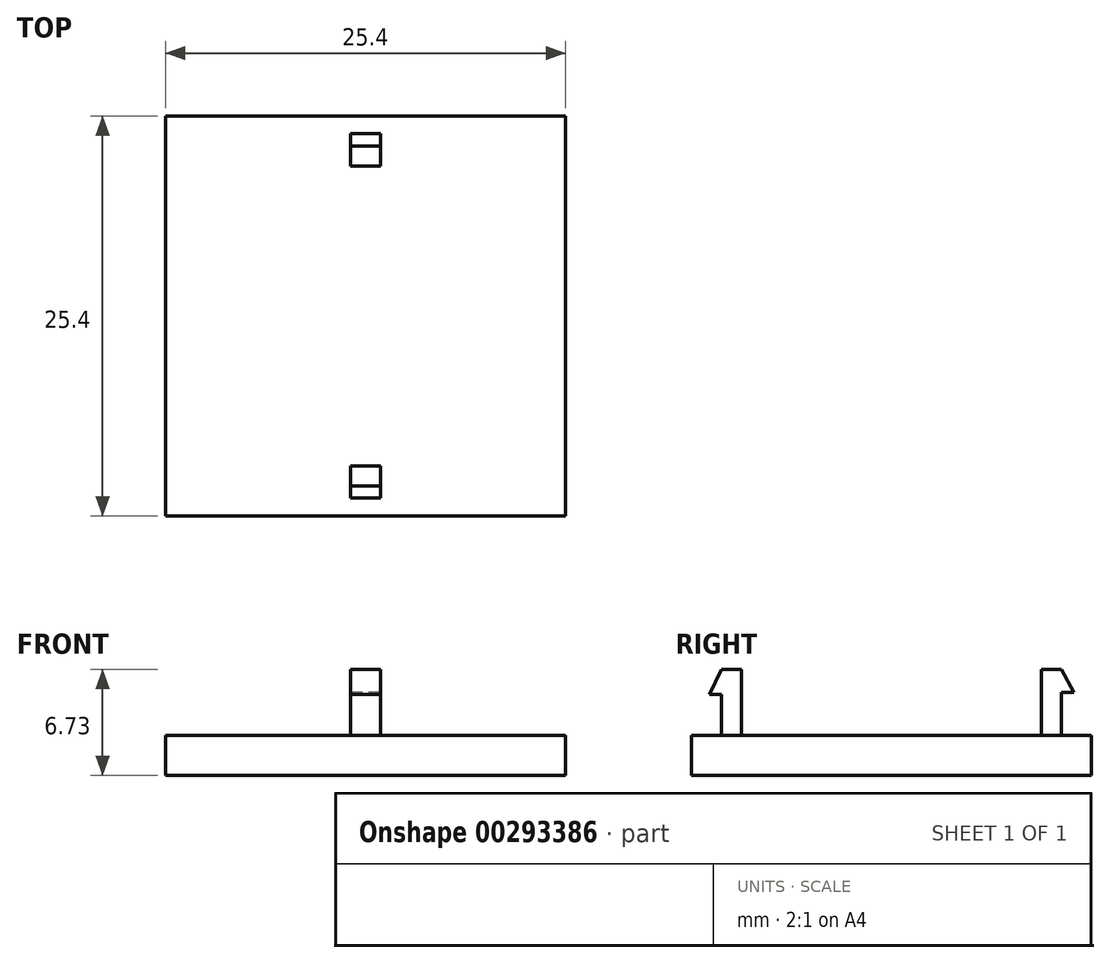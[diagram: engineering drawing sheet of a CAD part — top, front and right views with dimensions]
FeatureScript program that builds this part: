
annotation { "Feature Type Name" : "Feature", "Feature Type Description" : "" }
export const myFeature = defineFeature(function(context is Context, id is Id, definition is map)
    precondition{}
    {
        {
            var Q0;
            Q0=qCreatedBy(makeId("Top.planeOp"),FACE);
            var sketch = newSketch(context, id + "F0", { "sketchPlane" : qUnion([Q0])});
            skLineSegment(sketch, "E0.bottom", {"start": v(-50.58, 46.85) * mm, "end": v(-25.18, 46.85) * mm});
            skLineSegment(sketch, "E0.top", {"start": v(-50.58, 21.45) * mm, "end": v(-25.18, 21.45) * mm});
            skLineSegment(sketch, "E0.left", {"start": v(-50.58, 46.85) * mm, "end": v(-50.58, 21.45) * mm});
            skLineSegment(sketch, "E0.right", {"start": v(-25.18, 46.85) * mm, "end": v(-25.18, 21.45) * mm});
            skSolve(sketch);
        }
        {
            var Q0;
            Q0=qSketchRegion(id+"F0",true);
            extrude(context, id + "F1", {"entities" : qUnion([Q0]), "depth" : 2.54 * mm});
        }
        {
            var Q0;
            Q0=makeQuery(id+"F1.opExtrude","CAP_FACE",FACE,{"disambiguationData":[OSD([sQuery(id+"F0.wireOp",EDGE,"E0.bottom"),sQuery(id+"F0.wireOp",EDGE,"E0.top"),sQuery(id+"F0.wireOp",EDGE,"E0.left"),sQuery(id+"F0.wireOp",EDGE,"E0.right")])],"isStart":false});
            var sketch = newSketch(context, id + "F2", { "sketchPlane" : qUnion([Q0])});
            skLineSegment(sketch, "E1", {"start": v(-50.58, 45.76) * mm, "end": v(-37.88, 45.76) * mm});
            skLineSegment(sketch, "E2", {"start": v(-37.88, 46.85) * mm, "end": v(-37.88, 44.94) * mm});
            skLineSegment(sketch, "E3", {"start": v(-37.88, 21.45) * mm, "end": v(-37.88, 23.35) * mm});
            skLineSegment(sketch, "E4.bottom", {"start": v(-38.83, 24.62) * mm, "end": v(-36.93, 24.62) * mm});
            skLineSegment(sketch, "E4.top", {"start": v(-38.83, 23.35) * mm, "end": v(-36.93, 23.35) * mm});
            skLineSegment(sketch, "E4.left", {"start": v(-38.83, 24.62) * mm, "end": v(-38.83, 23.35) * mm});
            skLineSegment(sketch, "E4.right", {"start": v(-36.93, 24.62) * mm, "end": v(-36.93, 23.35) * mm});
            skLineSegment(sketch, "E5", {"start": v(-50.58, 24.04) * mm, "end": v(-38.83, 24.04) * mm});
            skLineSegment(sketch, "E6.bottom", {"start": v(-38.83, 44.94) * mm, "end": v(-36.93, 44.94) * mm});
            skLineSegment(sketch, "E6.top", {"start": v(-38.83, 43.67) * mm, "end": v(-36.93, 43.67) * mm});
            skLineSegment(sketch, "E6.left", {"start": v(-38.83, 44.94) * mm, "end": v(-38.83, 43.67) * mm});
            skLineSegment(sketch, "E6.right", {"start": v(-36.93, 44.94) * mm, "end": v(-36.93, 43.67) * mm});
            skLineSegment(sketch, "E7", {"start": v(-38.83, 44.3) * mm, "end": v(-50.58, 44.3) * mm});
            skSolve(sketch);
        }
        {
            var Q0;
            {var subQ1=sQuery(id+"F2.wireOp",EDGE,"E4.bottom");Q0=makeQuery(id+"F2.imprint","IMPRINT",FACE,{"disambiguationData":[TD([[makeQuery(id+"F2.imprint","IMPRINT",EDGE,{"derivedFrom":subQ1}),-1.0]])]});}
            extrude(context, id + "F3", {"entities" : qUnion([Q0]), "operationType" : NewBodyOperationType.ADD, "depth" : 4.2 * mm});
        }
        {
            var Q0;
            {var subQ4=sQuery(id+"F2.wireOp",EDGE,"E6.top");Q0=makeQuery(id+"F2.imprint","IMPRINT",FACE,{"disambiguationData":[TD([[makeQuery(id+"F2.imprint","IMPRINT",EDGE,{"derivedFrom":subQ4}),1.0]])]});}
            extrude(context, id + "F4", {"entities" : qUnion([Q0]), "operationType" : NewBodyOperationType.ADD, "depth" : 4.2 * mm});
        }
        {
            var Q0;
            Q0=makeQuery(id+"F4.opExtrude","SWEPT_FACE",FACE,{"disambiguationData":[OSD([sQuery(id+"F2.wireOp",EDGE,"E6.left")])]});
            var sketch = newSketch(context, id + "F5", { "sketchPlane" : qUnion([Q0])});
            skLineSegment(sketch, "E8", {"start": v(-44.94, 2.54) * mm, "end": v(-44.94, 5.27) * mm});
            skLineSegment(sketch, "E9", {"start": v(-44.94, 6.73) * mm, "end": v(-45.73, 5.27) * mm});
            skLineSegment(sketch, "E10", {"start": v(-45.73, 5.27) * mm, "end": v(-44.94, 5.27) * mm});
            skSolve(sketch);
        }
        {
            var Q0;
            Q0=makeQuery(id+"F3.opExtrude","SWEPT_FACE",FACE,{"disambiguationData":[OSD([sQuery(id+"F2.wireOp",EDGE,"E4.left")])]});
            var sketch = newSketch(context, id + "F6", { "sketchPlane" : qUnion([Q0])});
            skLineSegment(sketch, "E11", {"start": v(-23.35, 2.54) * mm, "end": v(-23.35, 5.14) * mm});
            skLineSegment(sketch, "E12", {"start": v(-23.35, 5.14) * mm, "end": v(-22.6, 5.14) * mm});
            skLineSegment(sketch, "E13", {"start": v(-22.6, 5.14) * mm, "end": v(-23.35, 6.73) * mm});
            skSolve(sketch);
        }
        {
            var Q0;
            Q0=qSketchRegion(id+"F6",true);
            var Q1;
            {var subQ0=sQuery(id+"F6.wireOp",EDGE,"E12");Q1=makeQuery(id+"F6.imprint","IMPRINT",FACE,{"disambiguationData":[TD([[makeQuery(id+"F6.imprint","IMPRINT",EDGE,{"derivedFrom":subQ0}),1.0]])]});}
            var Q2;
            {var subQ0=sQuery(id+"F5.wireOp",EDGE,"E9");Q2=makeQuery(id+"F5.imprint","IMPRINT",FACE,{"disambiguationData":[TD([[makeQuery(id+"F5.imprint","IMPRINT",EDGE,{"derivedFrom":subQ0}),1.0]])]});}
            extrude(context, id + "F7", {"entities" : qUnion([Q0, Q1, Q2]), "operationType" : NewBodyOperationType.ADD, "oppositeDirection" : true, "depth" : 1.9 * mm});
        }
    });
